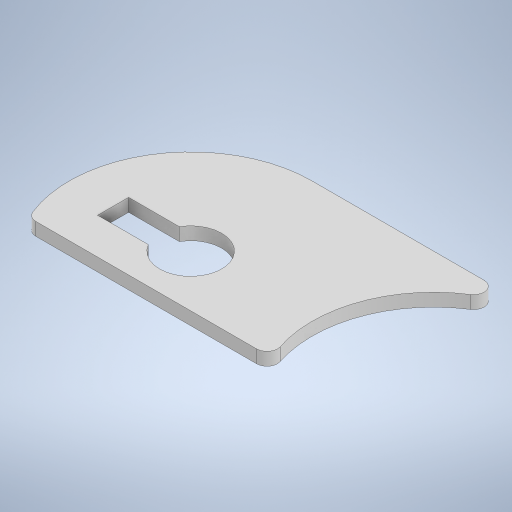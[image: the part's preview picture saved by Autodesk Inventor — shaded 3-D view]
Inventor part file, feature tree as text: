
AUTODESK INVENTOR PART (.ipt)
format: ipt  version: 2024.1 (Build 281209000, 209)  size: 247,296 bytes
history: native  units: mm
features: other x1, extrude x1, fillet x1, sketch x1
ambient origin geometry x8: Origin, YZ Plane, XZ Plane, XY Plane, X Axis, Y Axis, Z Axis, Center Point
bodies: Body1 (feature_tree)
feature tree (4):
  other  "ソリッド1"
  extrude  "押し出し1"  Depth=12.0mm
  fillet  "フィレット2"  Radius=15.0mm
  sketch  "スケッチ1"
